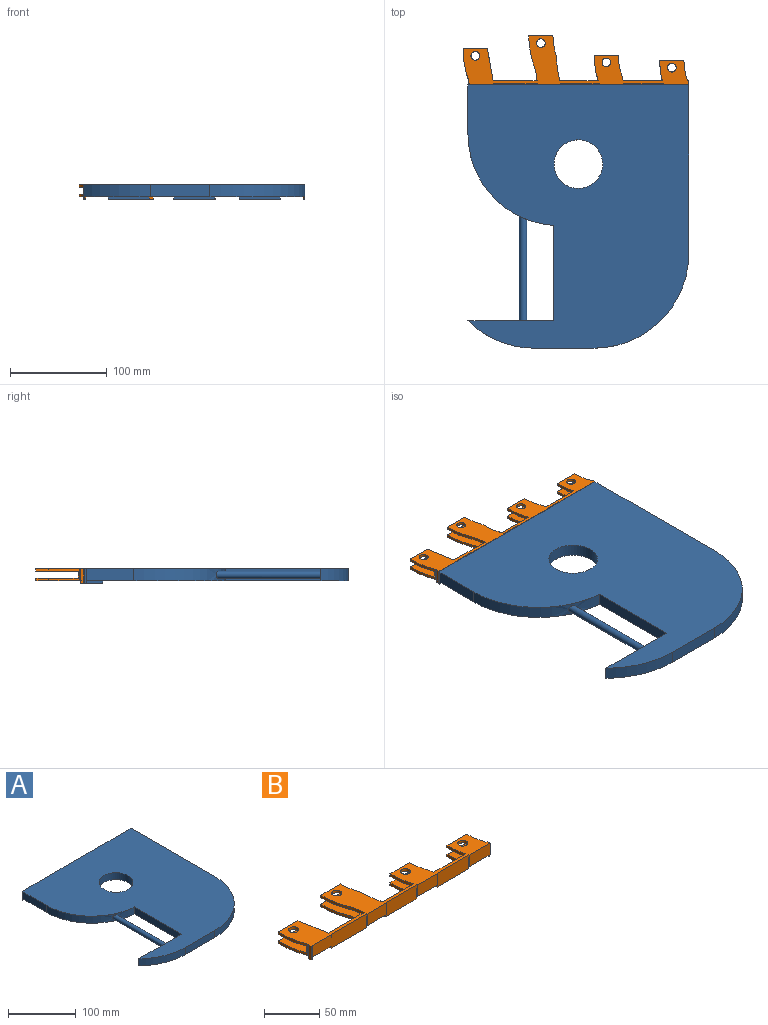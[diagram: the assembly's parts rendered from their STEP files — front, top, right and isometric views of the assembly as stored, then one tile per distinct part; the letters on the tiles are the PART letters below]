
ASSEMBLY  parts=2 mates=1
PART A: 45 faces, bbox 228.7x272.9x15.2 mm
  f0: plane 12.7x0.06mm, normal (-1,0,0), area 0.7mm2, adj f1,f2,f29,f43
  f1: plane 272.94x228.69mm, normal (0,0,1), area 47026.9mm2, adj f0,f3,f4,f5,f6,f7,f8,f9
  f2: plane 272.94x228.6mm, normal (0,0,-1), area 44601.4mm2, adj f0,f3,f4,f5,f6,f7,f8,f9
  f3: plane 12.7x0.06mm, normal (-1,0,0), area 0.7mm2, adj f1,f2,f39,f41
  f4: plane 12.7x0.06mm, normal (1,0,0), area 0.7mm2, adj f1,f2,f39,f42
  f5: plane 12.7x0.06mm, normal (-1,0,0), area 0.7mm2, adj f1,f2,f34,f42
  f6: plane 12.7x0.06mm, normal (1,0,0), area 0.7mm2, adj f1,f2,f34,f43
  f7: plane 12.7x0.06mm, normal (1,0,0), area 0.7mm2, adj f1,f2,f29,f44
  f8: plane 12.7x0.06mm, normal (-1,0,0), area 0.7mm2, adj f1,f2,f22,f44
  f9: plane 49.39x12.7mm, normal (-1,0,0), area 627.3mm2, adj f1,f2,f18,f24
  f10: plane 98.68x12.7mm, normal (-1,0,0), area 1253.3mm2, adj f1,f2,f11,f18
  f11: plane 88.92x12.7mm, normal (0,1,0), area 1083.7mm2, adj f1,f2,f10,f17,f19
  f12: plane 61.53x12.7mm, normal (0,-1,0), area 781.5mm2, adj f1,f2,f19,f20
  f13: plane 155.89x12.7mm, normal (1,0,0), area 1979.8mm2, adj f1,f2,f14,f20
  f14: plane 12.7x0.15mm, normal (0,1,0), area 1.9mm2, adj f1,f2,f13,f15
  f15: plane 18.94x12.7mm, normal (1,0,0), area 240.5mm2, adj f1,f2,f14,f41
  f16: cylinder r=25.15mm len=50.3mm, axis (0,0,-1), area 2006.8mm2, adj f1,f2
  f17: cylinder r=3.81mm len=108.12mm, axis (0,1,0), area 2547.4mm2, adj f11,f18
  f18: cylinder r=95.05mm len=94.85mm, axis (0,0,1), area 1768.5mm2, adj f1,f2,f9,f10,f17
  f19: cylinder r=98.11mm len=68.95mm, axis (0,0,1), area 971.1mm2, adj f1,f2,f11,f12
  f20: cylinder r=98.11mm len=98.11mm, axis (0,0,-1), area 1957.3mm2, adj f1,f2,f12,f13
  f21: plane 2.54x1.64mm, normal (1,0,0), area 4.2mm2, adj f2,f22,f24,f25
  f22: plane 15.24x0.09mm, normal (0,1,0), area 1.4mm2, adj f1,f8,f21,f23,f25
  f23: plane 15.24x1.64mm, normal (-1,0,0), area 25mm2, adj f1,f22,f24,f25
  f24: plane 15.24x0.09mm, normal (0,-1,0), area 1.4mm2, adj f1,f9,f21,f23,f25
  f25: plane 1.64x0.09mm, normal (0,0,-1), area 0.1mm2, adj f21,f22,f23,f24
  f26: plane 18.88x2.54mm, normal (-1,0,0), area 48mm2, adj f2,f27,f29,f30
  f27: plane 42.82x2.54mm, normal (0,-1,0), area 108.8mm2, adj f2,f26,f28,f30
  f28: plane 18.88x2.54mm, normal (1,0,0), area 48mm2, adj f2,f27,f29,f30
  f29: plane 42.82x15.24mm, normal (0,1,0), area 652.5mm2, adj f0,f1,f7,f26,f28,f30
  f30: plane 42.82x18.88mm, normal (0,0,-1), area 808.4mm2, adj f26,f27,f28,f29
  f31: plane 18.88x2.54mm, normal (-1,0,0), area 48mm2, adj f2,f32,f34,f35
  f32: plane 42.82x2.54mm, normal (0,-1,0), area 108.8mm2, adj f2,f31,f33,f35
  f33: plane 18.88x2.54mm, normal (1,0,0), area 48mm2, adj f2,f32,f34,f35
  f34: plane 42.82x15.24mm, normal (0,1,0), area 652.5mm2, adj f1,f5,f6,f31,f33,f35
  f35: plane 42.82x18.88mm, normal (0,0,-1), area 808.4mm2, adj f31,f32,f33,f34
  f36: plane 18.88x2.54mm, normal (-1,0,0), area 48mm2, adj f2,f37,f39,f40
  f37: plane 42.82x2.54mm, normal (0,-1,0), area 108.8mm2, adj f2,f36,f38,f40
  f38: plane 18.88x2.54mm, normal (1,0,0), area 48mm2, adj f2,f37,f39,f40
  f39: plane 42.82x15.24mm, normal (0,1,0), area 652.5mm2, adj f1,f3,f4,f36,f38,f40
  f40: plane 42.82x18.88mm, normal (0,0,-1), area 808.4mm2, adj f36,f37,f38,f39
  f41: plane 25x12.7mm, normal (0,1,0), area 317.5mm2, adj f1,f2,f3,f15
  f42: plane 25x12.7mm, normal (0,1,0), area 317.5mm2, adj f1,f2,f4,f5
  f43: plane 25x12.7mm, normal (0,1,0), area 317.5mm2, adj f0,f1,f2,f6
  f44: plane 25x12.7mm, normal (0,1,0), area 317.5mm2, adj f1,f2,f7,f8
PART B: 92 faces, bbox 233.5x50.4x15.2 mm
  f0: plane 3.31x1.4mm, normal (0,0,-1), area 2.8mm2, adj f35,f36,f38,f42,f43
  f1: plane 25.81x7.13mm, normal (0,1,0), area 184mm2, adj f2,f3,f44,f46
  f2: plane 27.81x18.7mm, normal (0,0,-1), area 409.3mm2, adj f1,f17,f34,f44,f46
  f3: plane 27.81x18.7mm, normal (0,0,1), area 409.3mm2, adj f1,f44,f45,f46,f48
  f4: plane 41.34x3.31mm, normal (0,0,-1), area 134mm2, adj f33,f39,f47,f49
  f5: plane 26.08x7.13mm, normal (0,1,0), area 185.8mm2, adj f6,f7,f50,f53
  f6: plane 29.33x23.78mm, normal (0,0,-1), area 541.5mm2, adj f5,f18,f31,f32,f50,f53
  f7: plane 29.33x23.78mm, normal (0,0,1), area 541.5mm2, adj f5,f50,f51,f52,f53,f55
  f8: plane 40.75x3.31mm, normal (0,0,-1), area 132mm2, adj f30,f40,f54,f56
  f9: plane 23.14x7.13mm, normal (0,1,0), area 164.9mm2, adj f10,f11,f57,f63
  f10: plane 44.1x31.6mm, normal (0,0,-1), area 1021.3mm2, adj f9,f19,f25,f26,f27,f28,f29,f57
  f11: plane 44.1x31.6mm, normal (0,0,1), area 1021.3mm2, adj f9,f57,f58,f59,f60,f61,f62,f63
  f12: plane 45.58x3.31mm, normal (0,0,-1), area 149.8mm2, adj f24,f41,f64,f65,f68
  f13: plane 30.98x30.51mm, normal (0,0,1), area 749.8mm2, adj f14,f67,f69,f70,f71
  f14: plane 25.6x7.13mm, normal (0,1,0), area 182.5mm2, adj f13,f15,f69,f71
  f15: plane 30.98x30.51mm, normal (0,0,-1), area 749.8mm2, adj f14,f20,f23,f69,f71
  f16: plane 3.31x1.35mm, normal (0,0,-1), area 2.9mm2, adj f21,f22,f37,f74
  f17: cylinder r=4.48mm len=8.97mm, axis (0,0,-1), area 78.3mm2, adj f2,f87
  f18: cylinder r=4.48mm len=8.97mm, axis (0,0,-1), area 78.3mm2, adj f6,f87
  f19: cylinder r=4.48mm len=8.97mm, axis (0,0,-1), area 78.3mm2, adj f10,f87
  f20: cylinder r=4.48mm len=8.97mm, axis (0,0,-1), area 78.3mm2, adj f15,f87
  f21: plane 15.24x3.31mm, normal (-1,0,0), area 50.4mm2, adj f16,f22,f37,f87
  f22: plane 15.24x0.33mm, normal (0,1,0), area 5.1mm2, adj f16,f21,f73,f74,f87
  f23: plane 24.99x2.78mm, normal (0,1,0), area 69.5mm2, adj f15,f69,f71,f87
  f24: plane 45.53x15.24mm, normal (0,1,0), area 693.8mm2, adj f12,f63,f64,f68,f69,f87
  f25: plane 2.78x0.26mm, normal (-0.94,-0.34,0), area 0.8mm2, adj f10,f26,f63,f87
  f26: cylinder r=88.63mm len=30.31mm, axis (0,0,-1), area 86mm2, adj f10,f25,f27,f87
  f27: plane 25x2.78mm, normal (0,1,0), area 69.5mm2, adj f10,f26,f28,f87
  f28: cylinder r=63.63mm len=21.76mm, axis (0,0,-1), area 61.7mm2, adj f10,f27,f29,f87
  f29: cylinder r=102.97mm len=22.24mm, axis (0,0,1), area 62.4mm2, adj f10,f28,f57,f87
  f30: plane 39.65x15.24mm, normal (0,1,0), area 604.3mm2, adj f8,f53,f54,f56,f57,f87
  f31: plane 25x2.78mm, normal (0,1,0), area 69.5mm2, adj f6,f32,f53,f87
  f32: cylinder r=63.63mm len=21.76mm, axis (0,0,-1), area 61.7mm2, adj f6,f31,f50,f87
  f33: plane 40.46x15.24mm, normal (0,1,0), area 616.6mm2, adj f4,f46,f47,f49,f50,f87
  f34: plane 25x2.78mm, normal (0,1,0), area 69.5mm2, adj f2,f44,f46,f87
  f35: plane 15.24x1.4mm, normal (0,1,0), area 21.4mm2, adj f0,f36,f43,f44,f87
  f36: plane 15.24x3.31mm, normal (1,0,0), area 50.4mm2, adj f0,f35,f38,f87
  f37: plane 15.24x1.35mm, normal (0,-1,0), area 20.6mm2, adj f16,f21,f74,f83,f87
  f38: plane 15.24x0.31mm, normal (0,-1,0), area 4.7mm2, adj f0,f36,f42,f85,f87
  f39: plane 40.54x15.24mm, normal (0,-1,0), area 617.8mm2, adj f4,f47,f49,f76,f86,f87
  f40: plane 40.15x15.24mm, normal (0,-1,0), area 611.9mm2, adj f8,f54,f56,f77,f79,f87
  f41: plane 44.99x15.24mm, normal (0,-1,0), area 685.7mm2, adj f12,f65,f68,f80,f82,f87
  f42: plane 2.68x2.54mm, normal (-0.95,-0.31,0), area 7.2mm2, adj f0,f38,f43,f84
  f43: cylinder r=63.63mm len=2.54mm, axis (0,0,1), area 1.7mm2, adj f0,f35,f42,f84
  f44: cylinder r=63.63mm len=21.14mm, axis (0,0,-1), area 138.4mm2, adj f1,f2,f3,f34,f35,f45,f84,f87
  f45: plane 25x2.79mm, normal (0,1,0), area 69.9mm2, adj f3,f44,f46,f84
  f46: cylinder r=88.63mm len=21.14mm, axis (0,0,-1), area 136.8mm2, adj f1,f2,f3,f33,f34,f45,f84,f87
  f47: cylinder r=88.63mm len=3.31mm, axis (0,0,1), area 8.7mm2, adj f4,f33,f39,f84
  f48: cylinder r=4.48mm len=8.97mm, axis (0,0,-1), area 78.7mm2, adj f3,f84
  f49: plane 3.31x2.54mm, normal (-0.97,-0.24,0), area 8.6mm2, adj f4,f33,f39,f75
  f50: plane 12.7x4.45mm, normal (0.97,0.24,0), area 43.4mm2, adj f5,f6,f7,f32,f33,f51,f75,f87
  f51: cylinder r=63.63mm len=21.76mm, axis (0,0,-1), area 62.1mm2, adj f7,f50,f52,f75
  f52: plane 25x2.79mm, normal (0,1,0), area 69.8mm2, adj f7,f51,f53,f75
  f53: cylinder r=88.63mm len=26.22mm, axis (0,0,-1), area 166.4mm2, adj f5,f6,f7,f30,f31,f52,f75,f87
  f54: cylinder r=88.63mm len=3.31mm, axis (0,0,1), area 8.9mm2, adj f8,f30,f40,f75
  f55: cylinder r=4.48mm len=8.97mm, axis (0,0,-1), area 78.7mm2, adj f7,f75
  f56: cylinder r=78.85mm len=3.31mm, axis (0,0,1), area 8.5mm2, adj f8,f30,f40,f78
  f57: cylinder r=78.85mm len=12.7mm, axis (0,0,-1), area 32.2mm2, adj f9,f10,f11,f29,f30,f58,f78,f87
  f58: cylinder r=102.97mm len=22.24mm, axis (0,0,1), area 62.7mm2, adj f11,f57,f59,f78
  f59: cylinder r=63.63mm len=21.76mm, axis (0,0,-1), area 62.1mm2, adj f11,f58,f60,f78
  f60: plane 25x2.79mm, normal (0,1,0), area 69.8mm2, adj f11,f59,f61,f78
  f61: cylinder r=88.63mm len=30.31mm, axis (0,0,-1), area 86.4mm2, adj f11,f60,f62,f78
  f62: plane 2.79x0.26mm, normal (-0.94,-0.34,0), area 0.8mm2, adj f11,f61,f63,f78
  f63: cylinder r=53.85mm len=15.96mm, axis (0,0,-1), area 108.5mm2, adj f9,f10,f11,f24,f25,f62,f78,f87
  f64: cylinder r=53.85mm len=2.54mm, axis (0,0,1), area 6.2mm2, adj f12,f24,f65,f78
  f65: plane 2.54x0.86mm, normal (1,0,0), area 2.2mm2, adj f12,f41,f64,f78
  f66: cylinder r=4.48mm len=8.97mm, axis (0,0,-1), area 78.7mm2, adj f11,f78
  f67: cylinder r=4.48mm len=8.97mm, axis (0,0,-1), area 78.7mm2, adj f13,f81
  f68: plane 3.31x2.54mm, normal (-0.98,-0.17,0), area 8.5mm2, adj f12,f24,f41,f81
  f69: plane 33.42x12.7mm, normal (0.98,0.17,0), area 206.8mm2, adj f13,f14,f15,f23,f24,f70,f81,f87
  f70: plane 24.99x2.79mm, normal (0,1,0), area 69.8mm2, adj f13,f69,f71,f81
  f71: cylinder r=88.63mm len=32.21mm, axis (0,0,-1), area 192.3mm2, adj f13,f14,f15,f23,f70,f72,f81,f87
  f72: plane 12.7x0.32mm, normal (-0.94,-0.34,0), area 4.3mm2, adj f71,f73,f81,f87
  f73: cylinder r=53.85mm len=12.7mm, axis (0,0,-1), area 12mm2, adj f22,f72,f81,f87
  f74: cylinder r=53.85mm len=3.31mm, axis (0,0,1), area 8.8mm2, adj f16,f22,f37,f81
  f75: plane 30.85x30.09mm, normal (0,0,-1), area 704.7mm2, adj f49,f50,f51,f52,f53,f54,f55,f76
  f76: plane 12.7x0.56mm, normal (0.97,0.24,0), area 7.3mm2, adj f39,f75,f87,f90
  f77: cylinder r=88.63mm len=12.7mm, axis (0,0,-1), area 7.5mm2, adj f40,f75,f87,f90
  f78: plane 50.41x32.81mm, normal (0,0,-1), area 1170.2mm2, adj f56,f57,f58,f59,f60,f61,f62,f63
  f79: cylinder r=78.85mm len=12.7mm, axis (0,0,-1), area 7.2mm2, adj f40,f78,f87,f89
  f80: plane 12.7x0.56mm, normal (-1,0,0), area 7.1mm2, adj f41,f78,f87,f89
  f81: plane 37.29x31.63mm, normal (0,0,-1), area 908mm2, adj f67,f68,f69,f70,f71,f72,f73,f74
  f82: plane 12.7x0.56mm, normal (0.98,0.17,0), area 7.2mm2, adj f41,f81,f87,f88
  f83: cylinder r=53.85mm len=12.7mm, axis (0,0,-1), area 7.4mm2, adj f37,f81,f87,f88
  f84: plane 29.89x25.01mm, normal (0,0,-1), area 573.9mm2, adj f42,f43,f44,f45,f46,f47,f48,f85
  f85: plane 12.7x0.56mm, normal (0.95,0.31,0), area 7.5mm2, adj f38,f84,f87,f91
  f86: cylinder r=88.63mm len=12.7mm, axis (0,0,-1), area 7.4mm2, adj f39,f84,f87,f91
  f87: plane 233.49x50.41mm, normal (0,0,1), area 3778.4mm2, adj f17,f18,f19,f20,f21,f22,f23,f24
  f88: plane 24.68x12.7mm, normal (0,-1,0), area 313.5mm2, adj f81,f82,f83,f87
  f89: plane 24.13x12.7mm, normal (0,-1,0), area 306.4mm2, adj f78,f79,f80,f87
  f90: plane 25.59x12.7mm, normal (0,-1,0), area 325mm2, adj f75,f76,f77,f87
  f91: plane 26.29x12.7mm, normal (0,-1,0), area 333.9mm2, adj f84,f85,f86,f87
PLACE A t=(-81.79,-127.53,-12.12)mm
PLACE B t=(-77.99,-183.37,-12.12)mm
MATE fastened B.f91 <-> A.f41  axis (0,-1,0) through (32.37,18.41,0.58)mm
